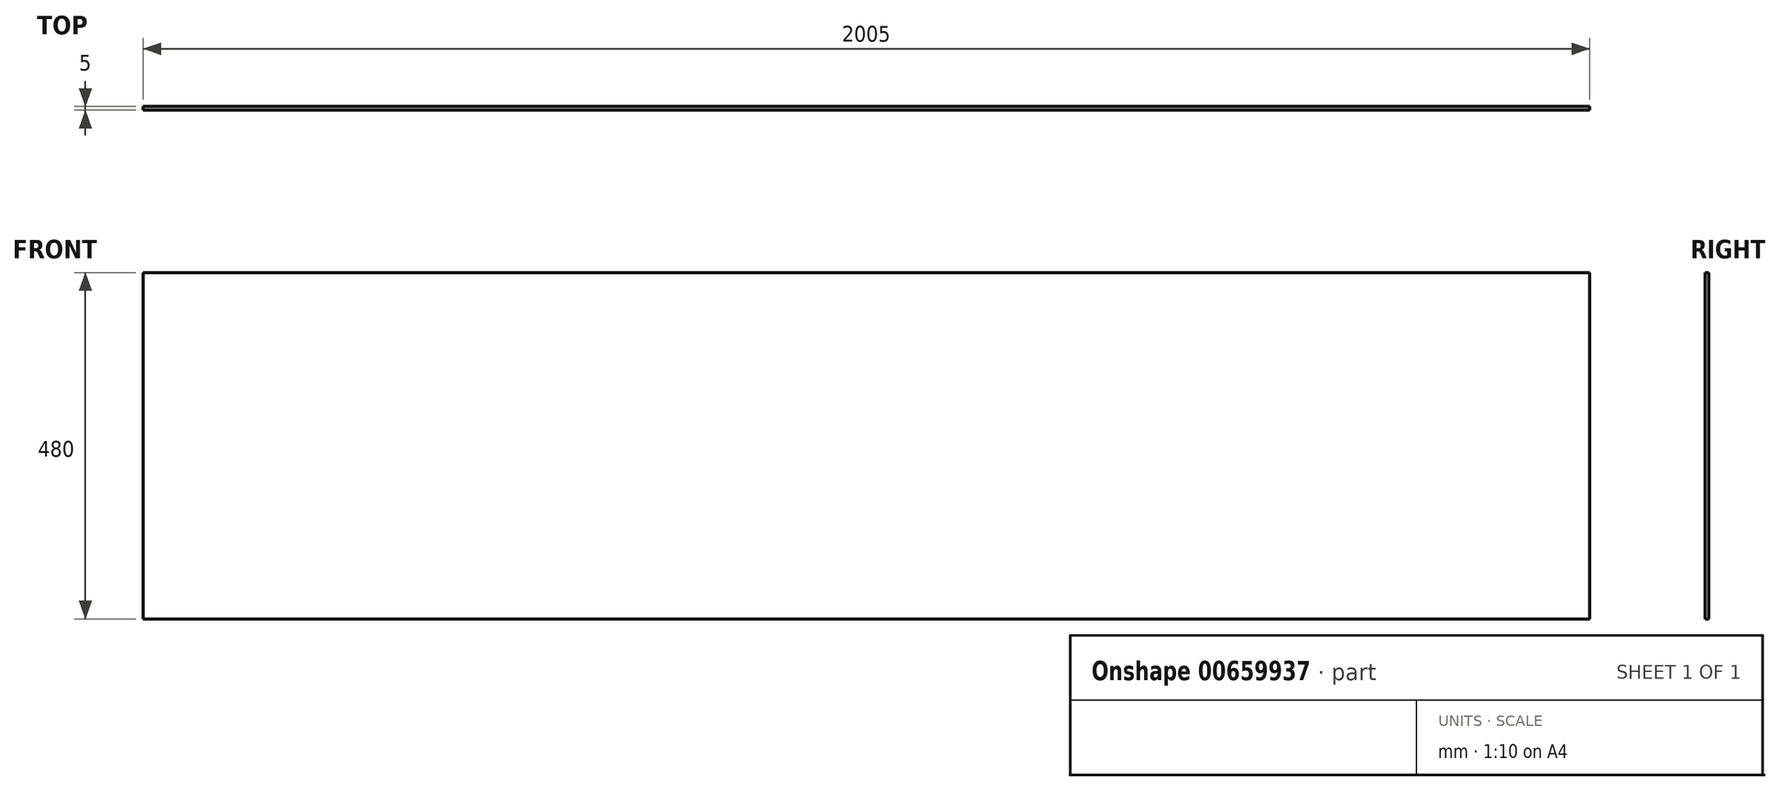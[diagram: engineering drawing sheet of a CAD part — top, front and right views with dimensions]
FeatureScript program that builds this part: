
annotation { "Feature Type Name" : "Feature", "Feature Type Description" : "" }
export const myFeature = defineFeature(function(context is Context, id is Id, definition is map)
    precondition{}
    {
        {
            var Q0;
            Q0=qCreatedBy(makeId("Front.planeOp"),FACE);
            var sketch = newSketch(context, id + "F0", { "sketchPlane" : qUnion([Q0])});
            skLineSegment(sketch, "E0.bottom", {"start": v(1002.5, 240) * mm, "end": v(-1002.5, 240) * mm});
            skLineSegment(sketch, "E0.top", {"start": v(1002.5, -240) * mm, "end": v(-1002.5, -240) * mm});
            skLineSegment(sketch, "E0.left", {"start": v(1002.5, 240) * mm, "end": v(1002.5, -240) * mm});
            skLineSegment(sketch, "E0.right", {"start": v(-1002.5, 240) * mm, "end": v(-1002.5, -240) * mm});
            skPoint(sketch, "E0.middle", {"position": v(0, 0) * mm});
            skSolve(sketch);
        }
        {
            var Q0;
            Q0=makeQuery(id+"F0.imprint","IMPRINT",FACE,{"disambiguationData":[TD([[makeQuery(id+"F0.imprint","IMPRINT",EDGE,{"derivedFrom":sQuery(id+"F0.wireOp",EDGE,"E0.bottom")}),1.0]])]});
            extrude(context, id + "F1", {"entities" : qUnion([Q0]), "endBound" : BoundingType.SYMMETRIC, "depth" : 5 * mm, "offsetDistance" : 25 * mm});
        }
    });
